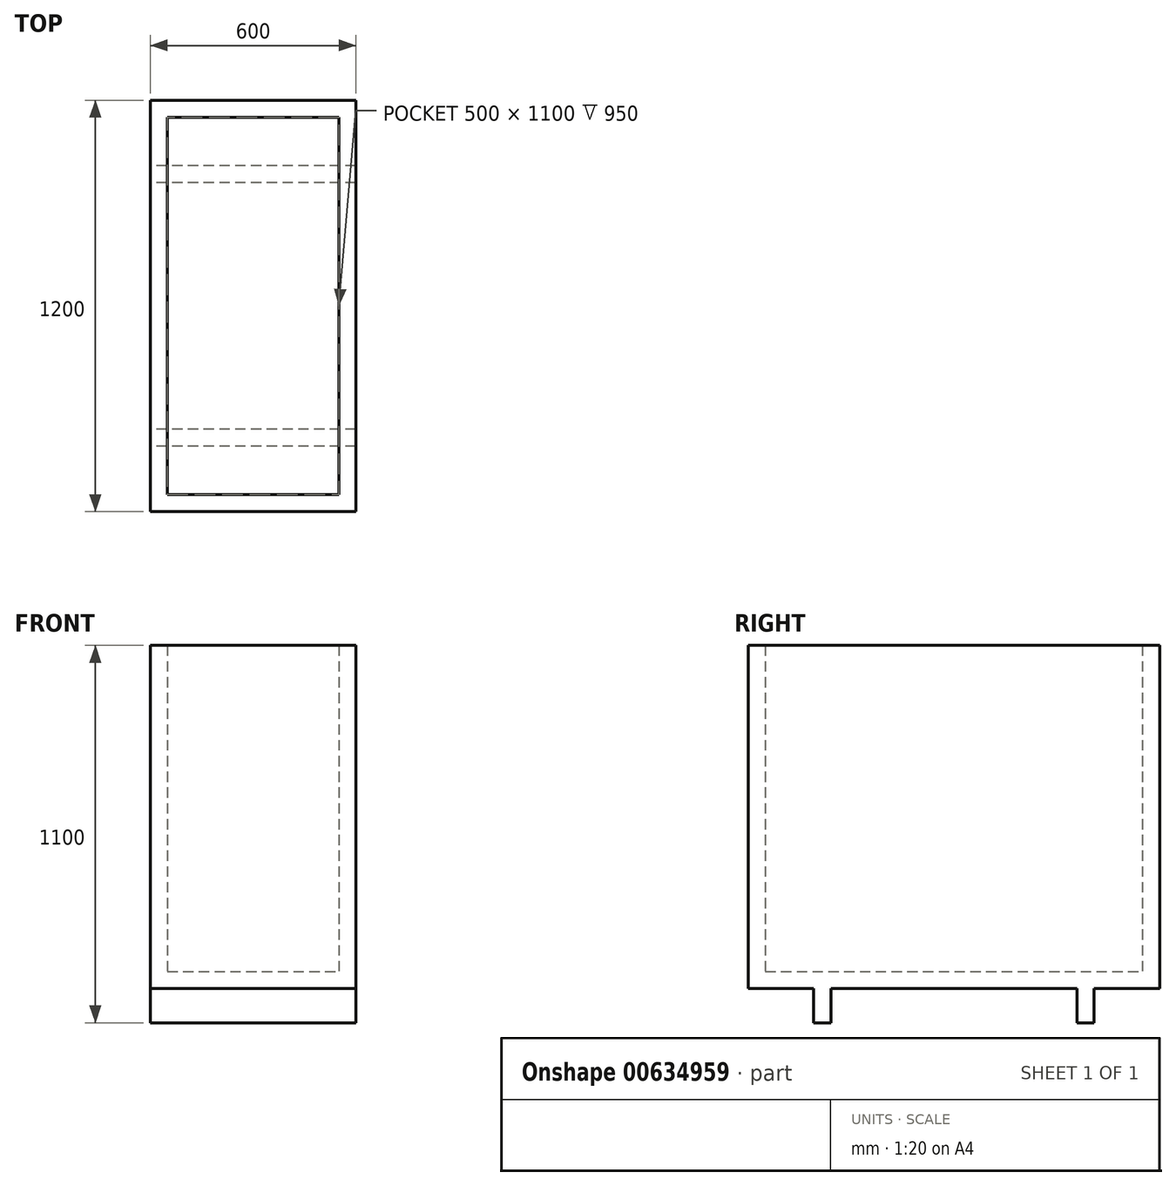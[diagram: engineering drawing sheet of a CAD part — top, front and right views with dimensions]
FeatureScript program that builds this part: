
annotation { "Feature Type Name" : "Feature", "Feature Type Description" : "" }
export const myFeature = defineFeature(function(context is Context, id is Id, definition is map)
    precondition{}
    {
        {
            var Q0;
            Q0=qCreatedBy(makeId("Top.planeOp"),FACE);
            var sketch = newSketch(context, id + "F0", { "sketchPlane" : qUnion([Q0])});
            skLineSegment(sketch, "E0.bottom", {"start": v(-300, -600) * mm, "end": v(300, -600) * mm});
            skLineSegment(sketch, "E0.top", {"start": v(-300, 600) * mm, "end": v(300, 600) * mm});
            skLineSegment(sketch, "E0.left", {"start": v(-300, -600) * mm, "end": v(-300, 600) * mm});
            skLineSegment(sketch, "E0.right", {"start": v(300, -600) * mm, "end": v(300, 600) * mm});
            skPoint(sketch, "E0.middle", {"position": v(0, 0) * mm});
            skSolve(sketch);
        }
        {
            var Q0;
            Q0 = qSketchRegion(id + "F0", true);
            extrude(context, id + "F1", {"entities" : qUnion([Q0]), "endBound" : BoundingType.SYMMETRIC, "depth" : 1000 * mm, "offsetDistance" : 25 * mm});
        }
        {
            var Q0;
            Q0=makeQuery(id+"F1.opExtrude","CAP_FACE",FACE,{"disambiguationData":[OSD([sQuery(id+"F0.wireOp",EDGE,"E0.bottom"),sQuery(id+"F0.wireOp",EDGE,"E0.top"),sQuery(id+"F0.wireOp",EDGE,"E0.left"),sQuery(id+"F0.wireOp",EDGE,"E0.right")])],"isStart":false});
            shell(context, id + "F2", {"entities" : qUnion([Q0]), "thickness" : 50 * mm});
        }
        {
            var Q0;
            Q0=qCreatedBy(makeId("Right.planeOp"),FACE);
            var sketch = newSketch(context, id + "F3", { "sketchPlane" : qUnion([Q0])});
            skLineSegment(sketch, "E1.0", {"start": v(-600, -500) * mm, "end": v(600, -500) * mm, "construction": true});
            skLineSegment(sketch, "E2.bottom", {"start": v(-409.02, -500) * mm, "end": v(-359.02, -500) * mm});
            skLineSegment(sketch, "E2.top", {"start": v(-409.02, -600) * mm, "end": v(-359.02, -600) * mm});
            skLineSegment(sketch, "E2.left", {"start": v(-409.02, -500) * mm, "end": v(-409.02, -600) * mm});
            skLineSegment(sketch, "E2.right", {"start": v(-359.02, -500) * mm, "end": v(-359.02, -600) * mm});
            skLineSegment(sketch, "E3", {"start": v(0, 0) * mm, "end": v(0, -967.28) * mm, "construction": true});
            skLineSegment(sketch, "E4.MirrorCS", {"start": v(359.02, -500) * mm, "end": v(359.02, -600) * mm});
            skLineSegment(sketch, "E5.MirrorCS", {"start": v(409.02, -500) * mm, "end": v(409.02, -600) * mm});
            skLineSegment(sketch, "E6.MirrorCS", {"start": v(409.02, -600) * mm, "end": v(359.02, -600) * mm});
            skLineSegment(sketch, "E7.MirrorCS", {"start": v(409.02, -500) * mm, "end": v(359.02, -500) * mm});
            skSolve(sketch);
        }
        {
            var Q0;
            Q0 = qSketchRegion(id + "F3", true);
            extrude(context, id + "F4", {"entities" : qUnion([Q0]), "operationType" : NewBodyOperationType.ADD, "endBound" : BoundingType.SYMMETRIC, "depth" : 600 * mm, "offsetDistance" : 25 * mm});
        }
    });
